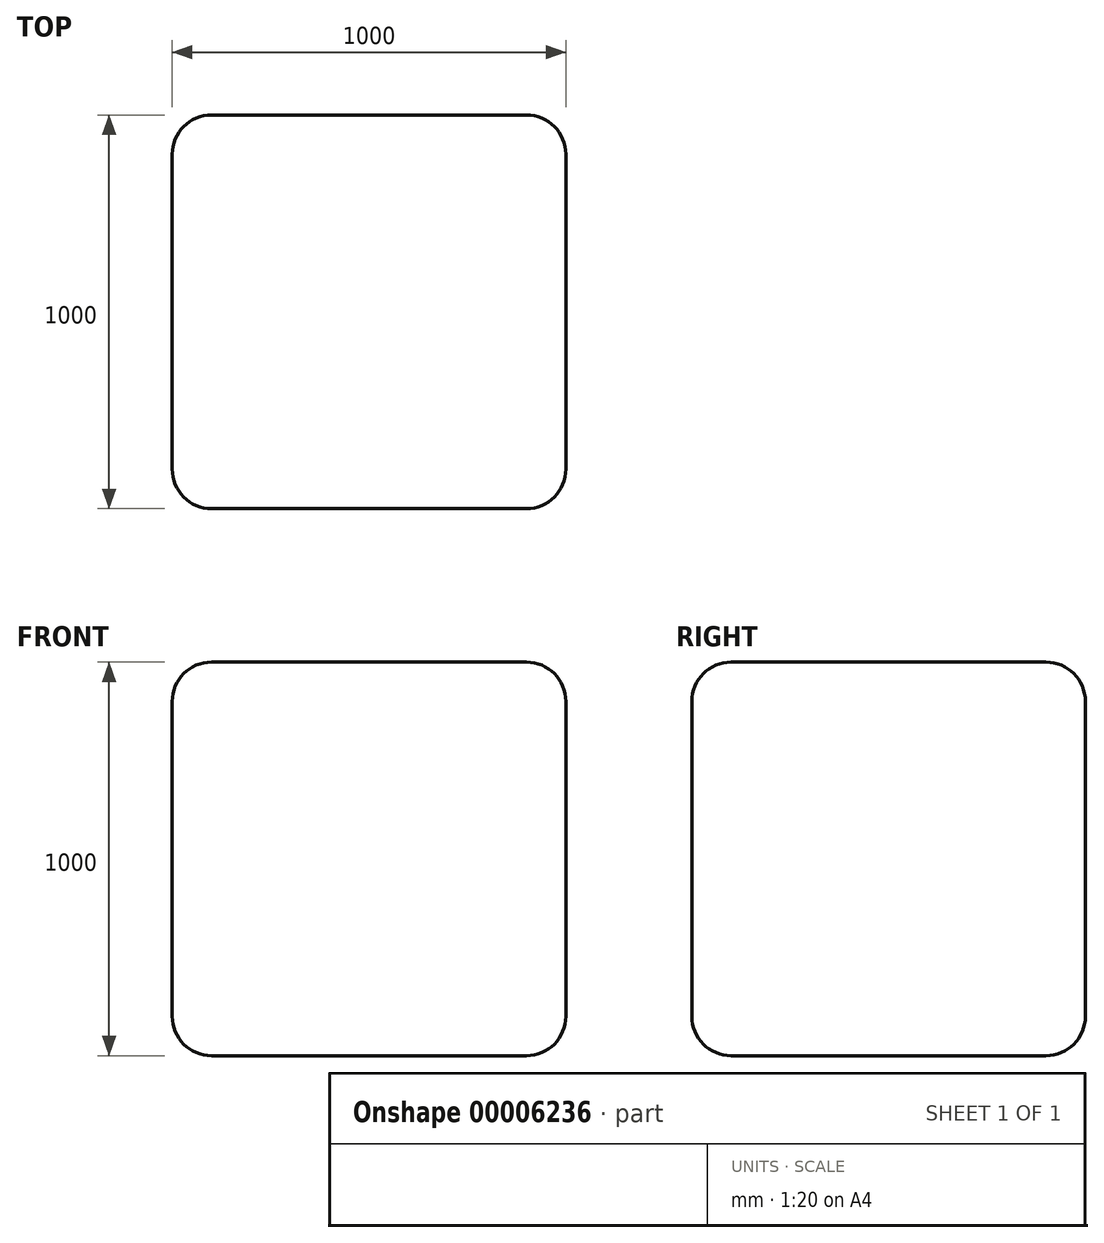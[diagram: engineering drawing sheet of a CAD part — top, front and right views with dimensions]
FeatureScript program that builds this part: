
annotation { "Feature Type Name" : "Feature", "Feature Type Description" : "" }
export const myFeature = defineFeature(function(context is Context, id is Id, definition is map)
    precondition{}
    {
        {
            var Q0;
            Q0=qCreatedBy(makeId("Top.planeOp"),FACE);
            var sketch = newSketch(context, id + "F0", { "sketchPlane" : qUnion([Q0])});
            skLineSegment(sketch, "E0.rect.bottom", {"start": v(500, 500) * mm, "end": v(-500, 500) * mm});
            skLineSegment(sketch, "E0.rect.top", {"start": v(500, -500) * mm, "end": v(-500, -500) * mm});
            skLineSegment(sketch, "E0.rect.left", {"start": v(500, 500) * mm, "end": v(500, -500) * mm});
            skLineSegment(sketch, "E0.rect.right", {"start": v(-500, 500) * mm, "end": v(-500, -500) * mm});
            skPoint(sketch, "E0.rect.middle", {"position": v(0, 0) * mm});
            skSolve(sketch);
        }
        {
            var Q0;
            Q0 = qSketchRegion(id + "F0", true);
            extrude(context, id + "F1", {"entities" : qUnion([Q0]), "depth" : 1000 * mm});
        }
        {
            var Q0;
            Q0=makeQuery(id+"F1.opExtrude","SWEPT_EDGE",EDGE,{"disambiguationData":[OSD([sQuery(id+"F0.wireOp",EDGE,"E0.rect.bottom"),sQuery(id+"F0.wireOp",EDGE,"E0.rect.left")])]});
            var Q1;
            Q1=makeQuery(id+"F1.opExtrude","SWEPT_EDGE",EDGE,{"disambiguationData":[OSD([sQuery(id+"F0.wireOp",EDGE,"E0.rect.bottom"),sQuery(id+"F0.wireOp",EDGE,"E0.rect.right")])]});
            var Q2;
            Q2=makeQuery(id+"F1.opExtrude","SWEPT_EDGE",EDGE,{"disambiguationData":[OSD([sQuery(id+"F0.wireOp",EDGE,"E0.rect.top"),sQuery(id+"F0.wireOp",EDGE,"E0.rect.left")])]});
            var Q3;
            Q3=makeQuery(id+"F1.opExtrude","SWEPT_EDGE",EDGE,{"disambiguationData":[OSD([sQuery(id+"F0.wireOp",EDGE,"E0.rect.top"),sQuery(id+"F0.wireOp",EDGE,"E0.rect.right")])]});
            var Q4;
            Q4=makeQuery(id+"F1.opExtrude","CAP_EDGE",EDGE,{"disambiguationData":[OSD([sQuery(id+"F0.wireOp",EDGE,"E0.rect.bottom")])],"isStart":false});
            var Q5;
            Q5=makeQuery(id+"F1.opExtrude","CAP_EDGE",EDGE,{"disambiguationData":[OSD([sQuery(id+"F0.wireOp",EDGE,"E0.rect.top")])],"isStart":true});
            var Q6;
            Q6=makeQuery(id+"F1.opExtrude","CAP_EDGE",EDGE,{"disambiguationData":[OSD([sQuery(id+"F0.wireOp",EDGE,"E0.rect.top")])],"isStart":false});
            var Q7;
            Q7=makeQuery(id+"F1.opExtrude","CAP_EDGE",EDGE,{"disambiguationData":[OSD([sQuery(id+"F0.wireOp",EDGE,"E0.rect.left")])],"isStart":true});
            var Q8;
            Q8=makeQuery(id+"F1.opExtrude","CAP_EDGE",EDGE,{"disambiguationData":[OSD([sQuery(id+"F0.wireOp",EDGE,"E0.rect.left")])],"isStart":false});
            var Q9;
            Q9=makeQuery(id+"F1.opExtrude","CAP_EDGE",EDGE,{"disambiguationData":[OSD([sQuery(id+"F0.wireOp",EDGE,"E0.rect.right")])],"isStart":false});
            var Q10;
            Q10=makeQuery(id+"F1.opExtrude","CAP_EDGE",EDGE,{"disambiguationData":[OSD([sQuery(id+"F0.wireOp",EDGE,"E0.rect.bottom")])],"isStart":true});
            var Q11;
            Q11=makeQuery(id+"F1.opExtrude","CAP_EDGE",EDGE,{"disambiguationData":[OSD([sQuery(id+"F0.wireOp",EDGE,"E0.rect.right")])],"isStart":true});
            fillet(context, id + "F2", {"entities" : qUnion([Q0, Q1, Q2, Q3, Q4, Q5, Q6, Q7, Q8, Q9, Q10, Q11]), "radius" : 100 * mm, "tangentPropagation" : true, "allowEdgeOverflow" : false});
        }
    });
